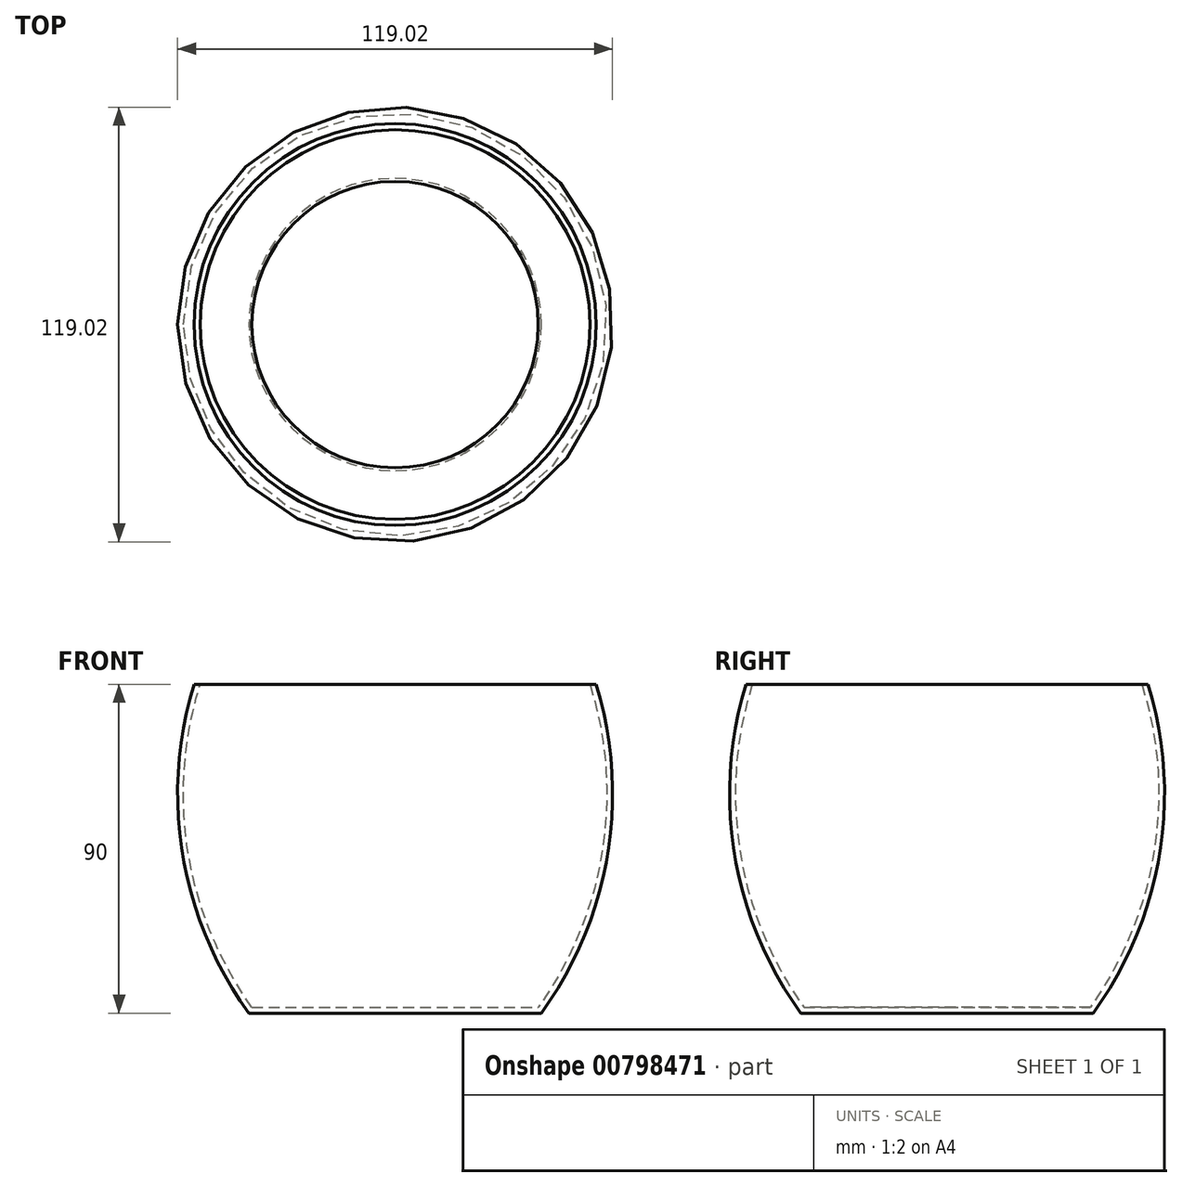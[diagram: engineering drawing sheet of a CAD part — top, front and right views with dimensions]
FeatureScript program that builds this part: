
annotation { "Feature Type Name" : "Feature", "Feature Type Description" : "" }
export const myFeature = defineFeature(function(context is Context, id is Id, definition is map)
    precondition{}
    {
        {
            var Q0;
            Q0=qCreatedBy(makeId("Front.planeOp"),FACE);
            var sketch = newSketch(context, id + "F0", { "sketchPlane" : qUnion([Q0])});
            skArc(sketch, "E0", {"start": v(40, 0) * mm, "mid": v(58.12, 43.23) * mm, "end": v(55, 90) * mm});
            skLineSegment(sketch, "E1", {"start": v(0, 0) * mm, "end": v(0, 90) * mm});
            skLineSegment(sketch, "E2", {"start": v(0, 90) * mm, "end": v(55, 90) * mm});
            skLineSegment(sketch, "E3", {"start": v(0, 0) * mm, "end": v(40, 0) * mm});
            skLineSegment(sketch, "E4", {"start": v(0, -53.22) * mm, "end": v(0, 115.55) * mm, "construction": true});
            skSolve(sketch);
        }
        {
            var Q0;
            Q0=makeQuery(id+"F0.imprint","IMPRINT",FACE,{"disambiguationData":[TD([[makeQuery(id+"F0.imprint","IMPRINT",EDGE,{"derivedFrom":sQuery(id+"F0.wireOp",EDGE,"E0")}),1.0]])]});
            var Q1;
            Q1=sQuery(id+"F0.wireOp",EDGE,"E4");
            revolve(context, id + "F1", {"surfaceOperationType" : NewSurfaceOperationType.NEW, "entities" : qUnion([Q0]), "axis" : qUnion([Q1]), "revolveType" : RevolveType.FULL});
        }
        {
            var Q0;
            Q0=makeQuery(id+"F1.opRevolve","SWEPT_FACE",FACE,{"disambiguationData":[OSD([sQuery(id+"F0.wireOp",EDGE,"E2")])]});
            shell(context, id + "F2", {"entities" : qUnion([Q0]), "thickness" : 1.6 * mm});
        }
    });
